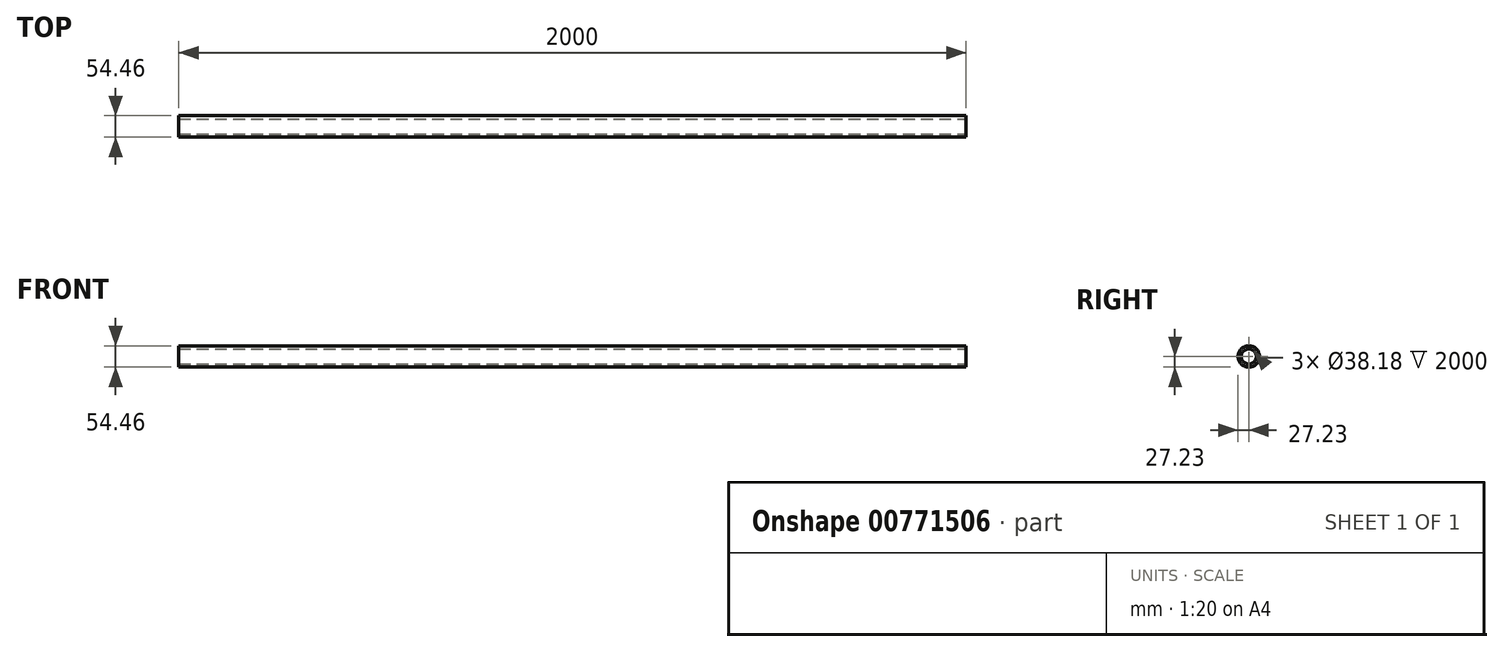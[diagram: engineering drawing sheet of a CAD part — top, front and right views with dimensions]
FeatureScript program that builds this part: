
annotation { "Feature Type Name" : "Feature", "Feature Type Description" : "" }
export const myFeature = defineFeature(function(context is Context, id is Id, definition is map)
    precondition{}
    {
        {
            var Q0;
            Q0=qCreatedBy(makeId("Front.planeOp"),FACE);
            var sketch = newSketch(context, id + "F0", { "sketchPlane" : qUnion([Q0])});
            skPoint(sketch, "E0", {"position": v(0, 0) * mm});
            skPoint(sketch, "E1.MirrorP", {"position": v(2000, 0) * mm});
            skLineSegment(sketch, "E2", {"start": v(0, 0) * mm, "end": v(2000, 0) * mm});
            skSolve(sketch);
        }
        {
            var Q0;
            Q0=qCreatedBy(makeId("Right.planeOp"),FACE);
            var sketch = newSketch(context, id + "F1", { "sketchPlane" : qUnion([Q0])});
            skCircle(sketch, "E3", {"center": v(0, 0) * mm, "radius": 27.23 * mm});
            skCircle(sketch, "E4", {"center": v(0, 0) * mm, "radius": 19.1 * mm});
            skSolve(sketch);
        }
        {
            var Q0;
            Q0=makeQuery(id+"F1.imprint","IMPRINT",FACE,{"disambiguationData":[TD([[makeQuery(id+"F1.imprint","IMPRINT",EDGE,{"derivedFrom":sQuery(id+"F1.wireOp",EDGE,"E3")}),1.0]])]});
            var Q1;
            Q1=sQuery(id+"F0.wireOp",EDGE,"E2");
            sweep(context, id + "F2", {"profiles" : qUnion([Q0]), "path" : qUnion([Q1])});
        }
    });
